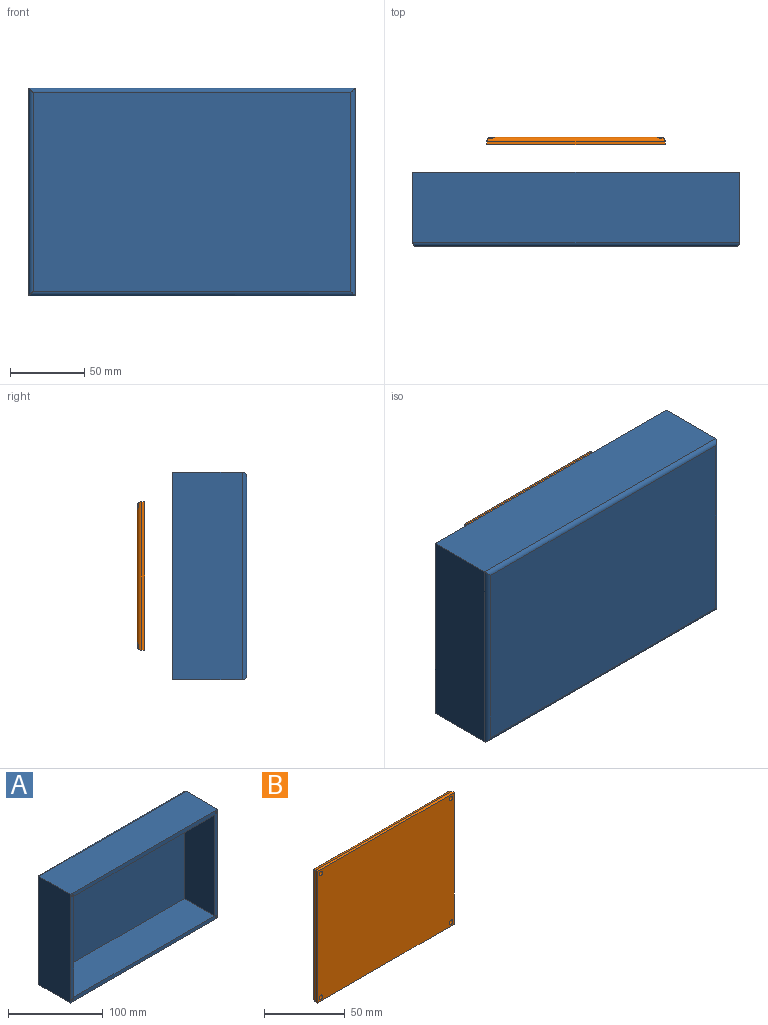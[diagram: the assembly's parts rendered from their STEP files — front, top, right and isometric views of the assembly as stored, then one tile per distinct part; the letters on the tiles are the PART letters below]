
ASSEMBLY  parts=2 mates=1
PART A: 26 faces, bbox 220x50x140 mm
  f0: plane 140x47mm, normal (1,0,0), area 6480mm2, adj f1,f2,f4,f10,f21,f23,f24,f25
  f1: plane 220x140mm, normal (0,-1,0), area 3480.4mm2, adj f0,f2,f3,f4,f6,f7,f8,f9
  f2: plane 220x47mm, normal (0,0,1), area 10340mm2, adj f0,f1,f3,f19
  f3: plane 140x47mm, normal (-1,0,0), area 6580mm2, adj f1,f2,f4,f20
  f4: plane 220x47mm, normal (0,0,-1), area 10340mm2, adj f0,f1,f3,f22
  f5: plane 214x134mm, normal (0,1,0), area 28676mm2, adj f19,f20,f21,f22
  f6: plane 210x45mm, normal (0,0,-1), area 9450mm2, adj f1,f7,f9,f10
  f7: plane 130x45mm, normal (1,0,0), area 5850mm2, adj f1,f6,f8,f10
  f8: plane 210x45mm, normal (0,0,1), area 9450mm2, adj f1,f7,f9,f10
  f9: plane 130x45mm, normal (-1,0,0), area 5750mm2, adj f1,f6,f8,f10,f23,f24,f25
  f10: plane 215x130mm, normal (0,-1,0), area 27350mm2, adj f0,f6,f7,f8,f9,f23,f25
  f11: cone r=0mm half-angle=59deg, axis (0,-1,0), area 5.7mm2, adj f12
  f12: cylinder r=1.25mm len=13.5mm, axis (0,-1,0), area 106mm2, adj f1,f11
  f13: cone r=0mm half-angle=59deg, axis (0,-1,0), area 5.7mm2, adj f14
  f14: cylinder r=1.25mm len=13.5mm, axis (0,-1,0), area 106mm2, adj f1,f13
  f15: cone r=0mm half-angle=59deg, axis (0,-1,0), area 5.7mm2, adj f16
  f16: cylinder r=1.25mm len=13.5mm, axis (0,-1,0), area 106mm2, adj f1,f15
  f17: cone r=0mm half-angle=59deg, axis (0,-1,0), area 5.7mm2, adj f18
  f18: cylinder r=1.25mm len=13.5mm, axis (0,-1,0), area 106mm2, adj f1,f17
  f19: cylinder r=3mm len=220mm, axis (-1,0,0), area 1026.5mm2, adj f2,f5,f20,f21
  f20: cylinder r=3mm len=140mm, axis (0,0,-1), area 649.5mm2, adj f3,f5,f19,f22
  f21: cylinder r=3mm len=140mm, axis (0,0,1), area 649.5mm2, adj f0,f5,f19,f22
  f22: cylinder r=3mm len=220mm, axis (1,0,0), area 1026.5mm2, adj f4,f5,f20,f21
  f23: plane 10x5mm, normal (0,0,1), area 50mm2, adj f0,f9,f10,f24
  f24: plane 10x5mm, normal (0,1,0), area 50mm2, adj f0,f9,f23,f25
  f25: plane 10x5mm, normal (0,0,-1), area 50mm2, adj f0,f9,f10,f24
PART B: 18 faces, bbox 120x5x100 mm
  f0: plane 120x2mm, normal (0,0,1), area 240mm2, adj f1,f3,f4,f14
  f1: plane 100x2mm, normal (-1,0,0), area 200mm2, adj f0,f2,f4,f15
  f2: plane 120x2mm, normal (0,0,-1), area 240mm2, adj f1,f3,f4,f17
  f3: plane 100x2mm, normal (1,0,0), area 200mm2, adj f0,f2,f4,f16
  f4: plane 120x100mm, normal (0,-1,0), area 11968.8mm2, adj f0,f1,f2,f3,f6,f8,f10,f12
  f5: plane 114x94mm, normal (0,1,0), area 10698.3mm2, adj f7,f9,f11,f13,f14,f15,f16,f17
  f6: cylinder r=1.57mm len=4.08mm, axis (0,1,0), area 40.3mm2, adj f4,f7
  f7: cone r=1.57mm half-angle=45deg, axis (0,1,0), area 9.9mm2, adj f5,f6,f14,f15
  f8: cylinder r=1.57mm len=4.08mm, axis (0,1,0), area 40.3mm2, adj f4,f9
  f9: cone r=1.57mm half-angle=45deg, axis (0,1,0), area 9.9mm2, adj f5,f8,f14,f16
  f10: cylinder r=1.57mm len=4.08mm, axis (0,1,0), area 40.3mm2, adj f4,f11
  f11: cone r=1.57mm half-angle=45deg, axis (0,1,0), area 9.9mm2, adj f5,f10,f16,f17
  f12: cylinder r=1.57mm len=4.08mm, axis (0,1,0), area 40.3mm2, adj f4,f13
  f13: cone r=1.57mm half-angle=45deg, axis (0,1,0), area 9.9mm2, adj f5,f12,f15,f17
  f14: cylinder r=3mm len=120mm, axis (-1,0,0), area 544.1mm2, adj f0,f5,f7,f9,f15,f16
  f15: cylinder r=3mm len=100mm, axis (0,0,-1), area 449.8mm2, adj f1,f5,f7,f13,f14,f17
  f16: cylinder r=3mm len=100mm, axis (0,0,1), area 449.8mm2, adj f3,f5,f9,f11,f14,f17
  f17: cylinder r=3mm len=120mm, axis (1,0,0), area 544.1mm2, adj f2,f5,f11,f13,f15,f16
PLACE A rot(axis=(1,0,0),180deg) t=(21.15,-111.94,-44.71)mm
PLACE B t=(21.45,-38.27,-44.71)mm
MATE slider B.f4 <-> A.f1  axis (0,-1,0) through (21.15,-43.27,-44.71)mm
